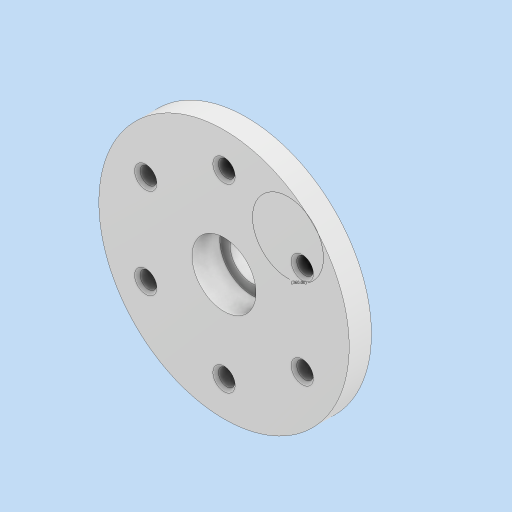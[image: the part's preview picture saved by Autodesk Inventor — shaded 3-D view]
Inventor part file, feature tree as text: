
AUTODESK INVENTOR PART (.ipt)
format: ipt  version: 2023 (Build 270158000, 158)  size: 230,400 bytes
history: native  units: in
note: dims shown in document units (in); Inventor stores cm internally (conversion verified against a paired STEP export)
features: sketch x4, plane x2, extrude x2, hole x2, other x2, chamfer x1, pattern_circular x1, projected_geometry x1
ambient origin geometry x8: Origin, YZ Plane, XZ Plane, XY Plane, X Axis, Y Axis, Z Axis, Center Point
bodies: Solid1 (feature_tree)
feature tree (15):
  plane  "Work Plane1"
  sketch  "Sketch1"  dims[d0=1.375in d1=2.5591in]
  extrude  "Extrusion1"  Depth=2.5591in
  plane  "Work Plane2"
  extrude  "Extrusion2"  Depth=0.2362in
  hole  "Hole1"  [1 undecoded]
  chamfer  "Chamfer1"  Distance=0.5906in
  hole  "Hole2"  [1 undecoded]
  pattern_circular  "Circular Pattern1"  [2 undecoded]
  sketch  "Sketch6"  dims[d20=0.6102in d21=0.2362in d22=0.9055in d23=0.3937in d24=90.0deg d25=0.315in d26=0.8108in d27=0.0394in d28=0.0787in d29=45.0deg d30=0.2559in d31=0.2362in d32=0.2756in d33=0.0787in d34=90.0deg d35=0.2362in d36=0.0in d37=1.0039in d38=1.9685in d39=360.0deg d41=1.9685in d43=360.0deg]
  sketch  "Sketch4"  dims[d2=3.5433in d3=0.2362in]
  sketch  "Sketch5"  dims[d4=2.3622in d6=360.0deg d8=0.315in d9=0.0in d10=0.5906in d11=0.0in]
  projected_geometry  "Projected Loop1"
  other  "Assembly1"
  other  "177x35x10 bearing:1"
note: 4 required parameter values undecoded (feature->parameter linkage not recoverable at this tier; creation-order binding heuristic only, values carry confidence <= 0.55)
